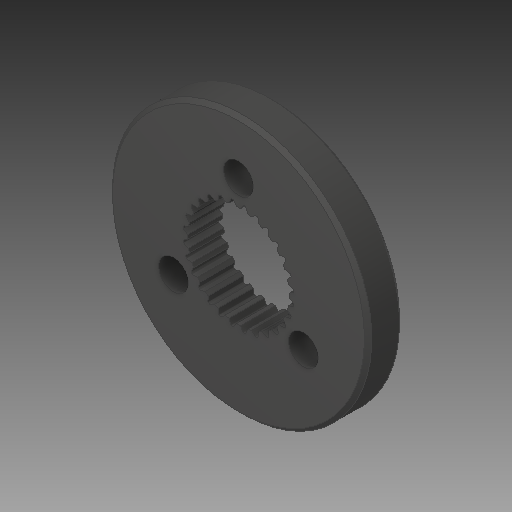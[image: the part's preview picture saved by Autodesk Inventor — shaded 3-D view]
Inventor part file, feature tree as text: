
AUTODESK INVENTOR PART (.ipt)
format: ipt  version: 2017 (Build 210142000, 142)  size: 274,944 bytes
history: native  units: in
note: dims shown in document units (in); Inventor stores cm internally (conversion verified against a paired STEP export)
features: chamfer x1
ambient origin geometry x8: Origin, YZ Plane, XZ Plane, XY Plane, X Axis, Y Axis, Z Axis, Center Point
bodies: Solid1 (feature_tree)
feature tree (1):
  chamfer  "Chamfer1"  [1 undecoded]
note: 1 required parameter value undecoded (feature->parameter linkage not recoverable at this tier; creation-order binding heuristic only, values carry confidence <= 0.55)
